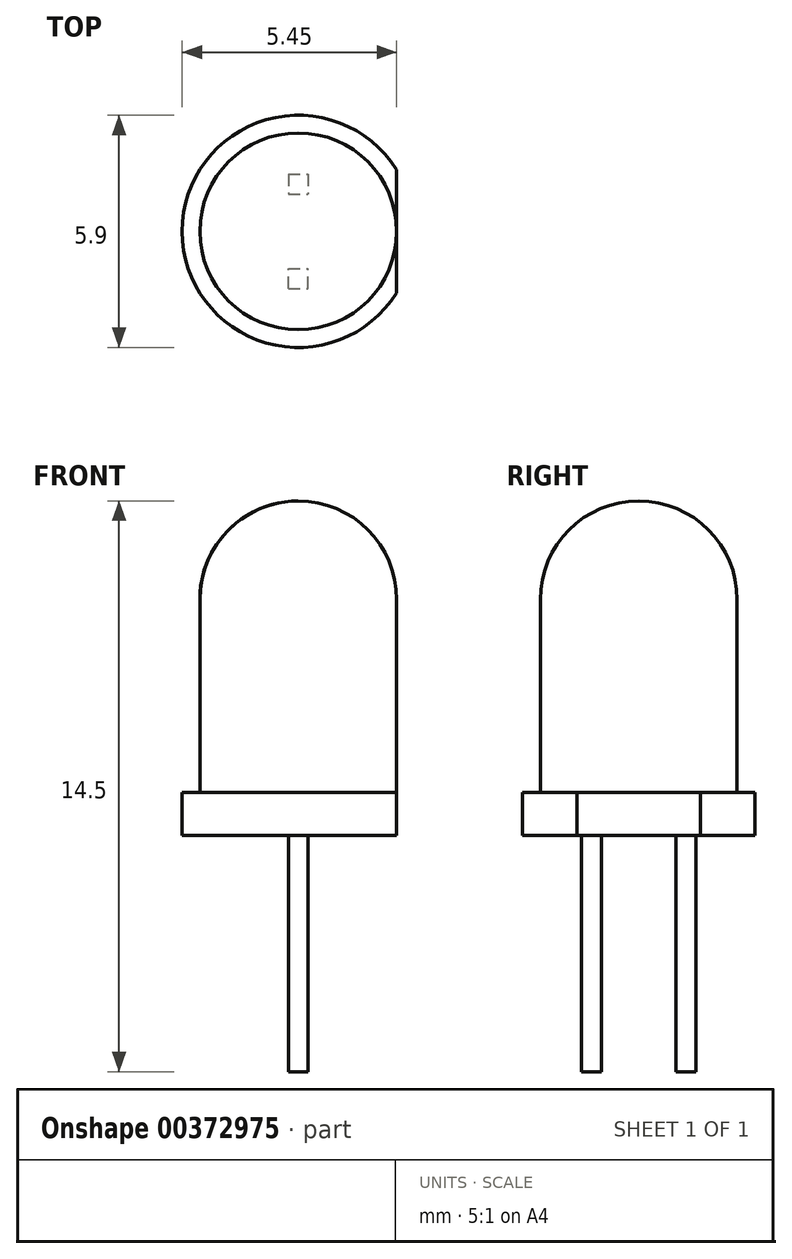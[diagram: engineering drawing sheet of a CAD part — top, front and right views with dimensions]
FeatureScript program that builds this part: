
annotation { "Feature Type Name" : "Feature", "Feature Type Description" : "" }
export const myFeature = defineFeature(function(context is Context, id is Id, definition is map)
    precondition{}
    {
        {
            var Q0;
            Q0=qCreatedBy(makeId("Front.planeOp"),FACE);
            var sketch = newSketch(context, id + "F0", { "sketchPlane" : qUnion([Q0])});
            skLineSegment(sketch, "E0", {"start": v(0, 0) * mm, "end": v(0, 6) * mm, "construction": true});
            skArc(sketch, "E1", {"start": v(0, 8.5) * mm, "mid": v(-1.77, 7.77) * mm, "end": v(-2.5, 6) * mm});
            skLineSegment(sketch, "E2", {"start": v(-2.5, 6) * mm, "end": v(-2.5, 1.1) * mm});
            skLineSegment(sketch, "E3", {"start": v(-2.5, 1.1) * mm, "end": v(-2.95, 1.1) * mm});
            skLineSegment(sketch, "E4", {"start": v(-2.95, 1.1) * mm, "end": v(-2.95, 0) * mm});
            skLineSegment(sketch, "E5", {"start": v(-2.95, 0) * mm, "end": v(0, 0) * mm});
            skLineSegment(sketch, "E6", {"start": v(0, 6) * mm, "end": v(0, 16.59) * mm, "construction": true});
            skLineSegment(sketch, "E7", {"start": v(0, 8.5) * mm, "end": v(0, 0) * mm});
            skSolve(sketch);
        }
        {
            var Q0;
            Q0 = qSketchRegion(id + "F0", true);
            var Q1;
            Q1=sQuery(id+"F0.wireOp",EDGE,"E6");
            revolve(context, id + "F1", {"surfaceOperationType" : NewSurfaceOperationType.NEW, "entities" : qUnion([Q0]), "axis" : qUnion([Q1]), "revolveType" : RevolveType.FULL});
        }
        {
            var Q0;
            Q0=makeQuery(id+"F1.opRevolve","SWEPT_FACE",FACE,{"disambiguationData":[OSD([sQuery(id+"F0.wireOp",EDGE,"E3")])]});
            var sketch = newSketch(context, id + "F2", { "sketchPlane" : qUnion([Q0])});
            skArc(sketch, "E8.0", {"start": v(2.5, -1.57) * mm, "mid": v(2.95, 0) * mm, "end": v(2.5, 1.57) * mm});
            skLineSegment(sketch, "E9", {"start": v(2.5, 1.57) * mm, "end": v(2.5, -1.57) * mm});
            skSolve(sketch);
        }
        {
            var Q0;
            Q0 = qSketchRegion(id + "F2", true);
            var Q1;
            Q1=makeQuery(id+"F1.opRevolve","SWEPT_FACE",FACE,{"disambiguationData":[OSD([sQuery(id+"F0.wireOp",EDGE,"E5")])]});
            extrude(context, id + "F3", {"entities" : qUnion([Q0]), "operationType" : NewBodyOperationType.REMOVE, "endBound" : BoundingType.UP_TO_SURFACE, "oppositeDirection" : true, "depth" : 25 * mm, "endBoundEntityFace" : qUnion([Q1]), "offsetDistance" : 25 * mm});
        }
        {
            var Q0;
            Q0=makeQuery(id+"F1.opRevolve","SWEPT_FACE",FACE,{"disambiguationData":[OSD([sQuery(id+"F0.wireOp",EDGE,"E5")])]});
            var sketch = newSketch(context, id + "F4", { "sketchPlane" : qUnion([Q0])});
            skLineSegment(sketch, "E10.bottom", {"start": v(-0.25, 1.45) * mm, "end": v(0.25, 1.45) * mm});
            skLineSegment(sketch, "E10.top", {"start": v(-0.25, 0.95) * mm, "end": v(0.25, 0.95) * mm});
            skLineSegment(sketch, "E10.left", {"start": v(-0.25, 1.45) * mm, "end": v(-0.25, 0.95) * mm});
            skLineSegment(sketch, "E10.right", {"start": v(0.25, 1.45) * mm, "end": v(0.25, 0.95) * mm});
            skLineSegment(sketch, "E11", {"start": v(0, 0) * mm, "end": v(-5.02, 0) * mm, "construction": true});
            skLineSegment(sketch, "E12", {"start": v(0, 0.95) * mm, "end": v(0, 0) * mm, "construction": true});
            skLineSegment(sketch, "E13.MirrorCS", {"start": v(-0.25, -0.95) * mm, "end": v(0.25, -0.95) * mm});
            skLineSegment(sketch, "E14.MirrorCS", {"start": v(-0.25, -1.45) * mm, "end": v(-0.25, -0.95) * mm});
            skLineSegment(sketch, "E15.MirrorCS", {"start": v(0.25, -1.45) * mm, "end": v(0.25, -0.95) * mm});
            skLineSegment(sketch, "E16.MirrorCS", {"start": v(-0.25, -1.45) * mm, "end": v(0.25, -1.45) * mm});
            skSolve(sketch);
        }
        {
            var Q0;
            Q0 = qSketchRegion(id + "F4", true);
            extrude(context, id + "F5", {"entities" : qUnion([Q0]), "operationType" : NewBodyOperationType.ADD, "depth" : 6 * mm, "offsetDistance" : 25 * mm});
        }
    });
